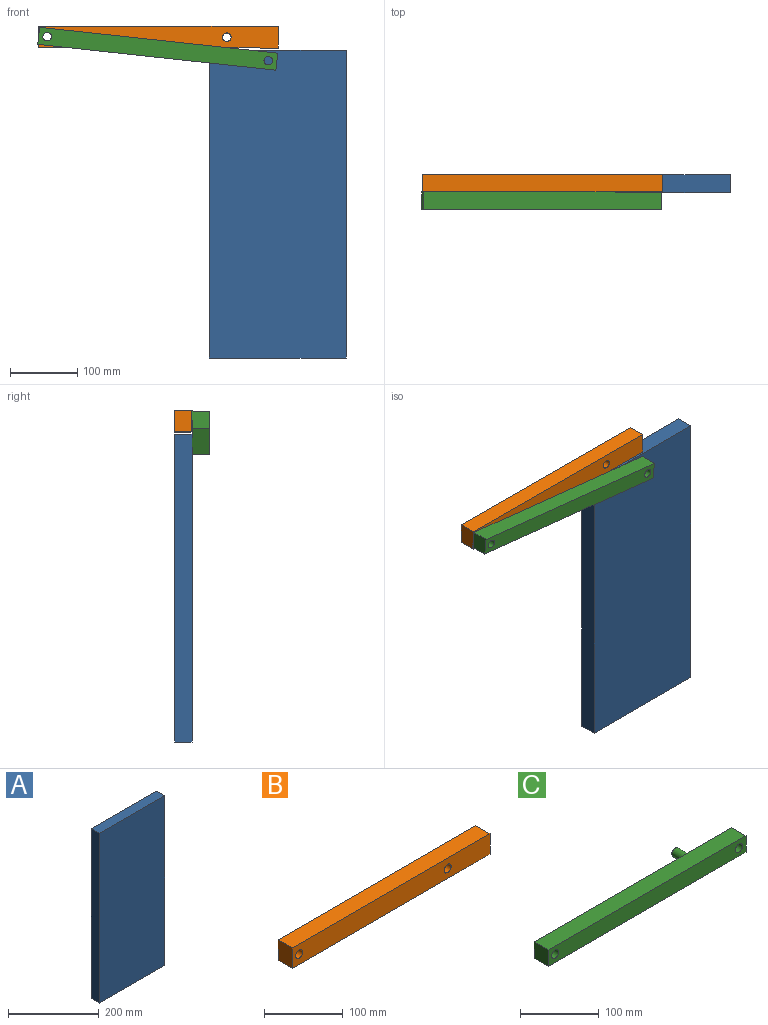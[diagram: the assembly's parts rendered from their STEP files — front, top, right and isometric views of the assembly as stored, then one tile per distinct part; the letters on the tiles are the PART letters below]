
ASSEMBLY  parts=3 mates=3
PART A: 6 faces, bbox 203.2x25.4x457.2 mm
  f0: plane 457.2x25.4mm, normal (1,0,0), area 11612.9mm2, adj f1,f3,f4,f5
  f1: plane 203.2x25.4mm, normal (0,0,1), area 5161.3mm2, adj f0,f2,f4,f5
  f2: plane 457.2x25.4mm, normal (-1,0,0), area 11612.9mm2, adj f1,f3,f4,f5
  f3: plane 203.2x25.4mm, normal (0,0,-1), area 5161.3mm2, adj f0,f2,f4,f5
  f4: plane 457.2x203.2mm, normal (0,-1,0), area 92903mm2, adj f0,f1,f2,f3
  f5: plane 457.2x203.2mm, normal (0,1,0), area 92903mm2, adj f0,f1,f2,f3
PART B: 8 faces, bbox 355.6x25.4x31.8 mm
  f0: plane 355.6x25.4mm, normal (0,0,-1), area 9032.2mm2, adj f1,f5,f6,f7
  f1: plane 31.75x25.4mm, normal (1,0,0), area 806.5mm2, adj f0,f2,f6,f7
  f2: plane 355.6x25.4mm, normal (0,0,1), area 9032.2mm2, adj f1,f5,f6,f7
  f3: cylinder r=6.35mm len=25.4mm, axis (0,1,0), area 1013.4mm2, adj f6,f7
  f4: cylinder r=6.35mm len=25.4mm, axis (0,1,0), area 1013.4mm2, adj f6,f7
  f5: plane 31.75x25.4mm, normal (-1,0,0), area 806.5mm2, adj f0,f2,f6,f7
  f6: plane 355.6x31.75mm, normal (0,-1,0), area 11036.9mm2, adj f0,f1,f2,f3,f4,f5
  f7: plane 355.6x31.75mm, normal (0,1,0), area 11036.9mm2, adj f0,f1,f2,f3,f4,f5
PART C: 10 faces, bbox 355.6x50.8x25.4 mm
  f0: plane 355.6x25.4mm, normal (0,0,-1), area 9032.2mm2, adj f1,f5,f6,f7
  f1: plane 25.4x25.4mm, normal (1,0,0), area 645.2mm2, adj f0,f2,f6,f7
  f2: plane 355.6x25.4mm, normal (0,0,1), area 9032.2mm2, adj f1,f5,f6,f7
  f3: cylinder r=6.35mm len=25.4mm, axis (0,1,0), area 1013.4mm2, adj f6,f7
  f4: cylinder r=6.35mm len=25.4mm, axis (0,1,0), area 1013.4mm2, adj f6,f7
  f5: plane 25.4x25.4mm, normal (-1,0,0), area 645.2mm2, adj f0,f2,f6,f7
  f6: plane 355.6x25.4mm, normal (0,-1,0), area 8778.9mm2, adj f0,f1,f2,f3,f4,f5
  f7: plane 355.6x25.4mm, normal (0,1,0), area 8652.2mm2, adj f0,f1,f2,f3,f4,f5,f9
  f8: plane 12.7x12.7mm, normal (0,1,0), area 126.7mm2, adj f9
  f9: cylinder r=6.35mm len=25.4mm, axis (0,-1,0), area 1013.4mm2, adj f7,f8
PLACE A t=(41.84,-134.7,59.24)mm fixed
PLACE B rot(axis=(0,1,0),0.2deg) t=(-59.4,-134.7,62.17)mm
PLACE C rot(axis=(0,1,0),6.2deg) t=(-62.73,-160.1,29.38)mm
MATE revolute B.f3 <-> C.f4  axis (0,-1,0) through (-402.26,-160.1,78.99)mm
MATE planar B.f6 <-> A.f4  axis (0,-1,0) through (-236.43,-160.1,78.53)mm
MATE planar C.f7 <-> A.f4  axis (0,1,0) through (-239.6,-160.1,61.34)mm
